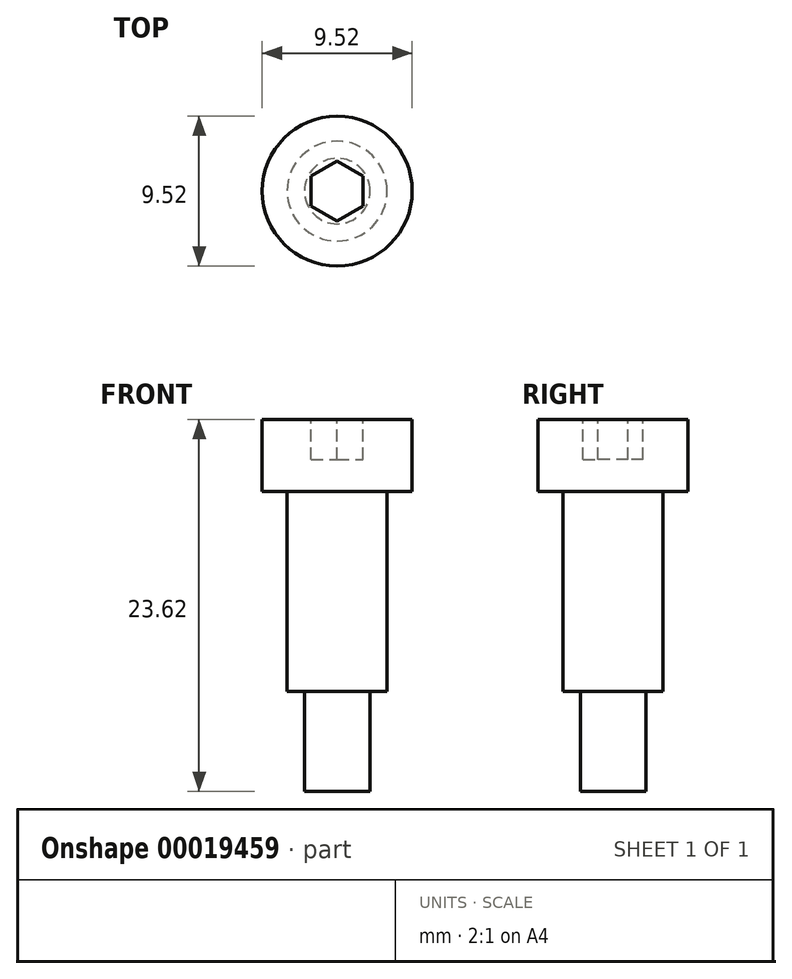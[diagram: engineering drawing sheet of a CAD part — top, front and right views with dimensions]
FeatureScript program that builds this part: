
annotation { "Feature Type Name" : "Feature", "Feature Type Description" : "" }
export const myFeature = defineFeature(function(context is Context, id is Id, definition is map)
    precondition{}
    {
        {
            var Q0;
            Q0=qCreatedBy(makeId("Front.planeOp"),FACE);
            var sketch = newSketch(context, id + "F0", { "sketchPlane" : qUnion([Q0])});
            skLineSegment(sketch, "E0", {"start": v(0, 32.08) * mm, "end": v(0, -25.73) * mm, "construction": true});
            skLineSegment(sketch, "E1", {"start": v(0, 23.62) * mm, "end": v(4.76, 23.62) * mm});
            skLineSegment(sketch, "E2", {"start": v(4.76, 23.62) * mm, "end": v(4.76, 19.05) * mm});
            skLineSegment(sketch, "E3", {"start": v(4.76, 19.05) * mm, "end": v(3.18, 19.05) * mm});
            skLineSegment(sketch, "E4", {"start": v(3.18, 19.05) * mm, "end": v(3.18, 6.35) * mm});
            skLineSegment(sketch, "E5", {"start": v(3.18, 6.35) * mm, "end": v(2.08, 6.35) * mm});
            skLineSegment(sketch, "E6", {"start": v(2.08, 6.35) * mm, "end": v(2.08, 0) * mm});
            skLineSegment(sketch, "E7", {"start": v(2.08, 0) * mm, "end": v(0, 0) * mm});
            skLineSegment(sketch, "E8", {"start": v(0, 0) * mm, "end": v(0, 23.62) * mm});
            skSolve(sketch);
        }
        {
            var Q0;
            Q0 = qSketchRegion(id + "F0", true);
            var Q1;
            Q1=sQuery(id+"F0.wireOp",EDGE,"E0");
            revolve(context, id + "F1", {"entities" : qUnion([Q0]), "axis" : qUnion([Q1]), "revolveType" : RevolveType.FULL});
        }
        {
            var Q0;
            Q0=makeQuery(id+"F1.opRevolve","SWEPT_FACE",FACE,{"disambiguationData":[OSD([sQuery(id+"F0.wireOp",EDGE,"E1")])]});
            var sketch = newSketch(context, id + "F2", { "sketchPlane" : qUnion([Q0])});
            skCircle(sketch, "E9.cCircle", {"center": v(0, 0) * mm, "radius": 1.65 * mm, "construction": true});
            skLineSegment(sketch, "E9.0", {"start": v(1.65, 0.95) * mm, "end": v(1.65, -0.95) * mm});
            skLineSegment(sketch, "E9.1", {"start": v(1.65, -0.95) * mm, "end": v(0, -1.9) * mm});
            skLineSegment(sketch, "E9.2", {"start": v(0, -1.9) * mm, "end": v(-1.65, -0.95) * mm});
            skLineSegment(sketch, "E9.3", {"start": v(-1.65, -0.95) * mm, "end": v(-1.65, 0.95) * mm});
            skLineSegment(sketch, "E9.4", {"start": v(-1.65, 0.95) * mm, "end": v(0, 1.9) * mm});
            skLineSegment(sketch, "E9.5", {"start": v(0, 1.9) * mm, "end": v(1.65, 0.95) * mm});
            skPoint(sketch, "E9.0.midPoint", {"position": v(1.65, 0) * mm});
            skSolve(sketch);
        }
        {
            var Q0;
            Q0 = qSketchRegion(id + "F2", true);
            extrude(context, id + "F3", {"entities" : qUnion([Q0]), "operationType" : NewBodyOperationType.REMOVE, "oppositeDirection" : true, "depth" : 2.54 * mm});
        }
    });
